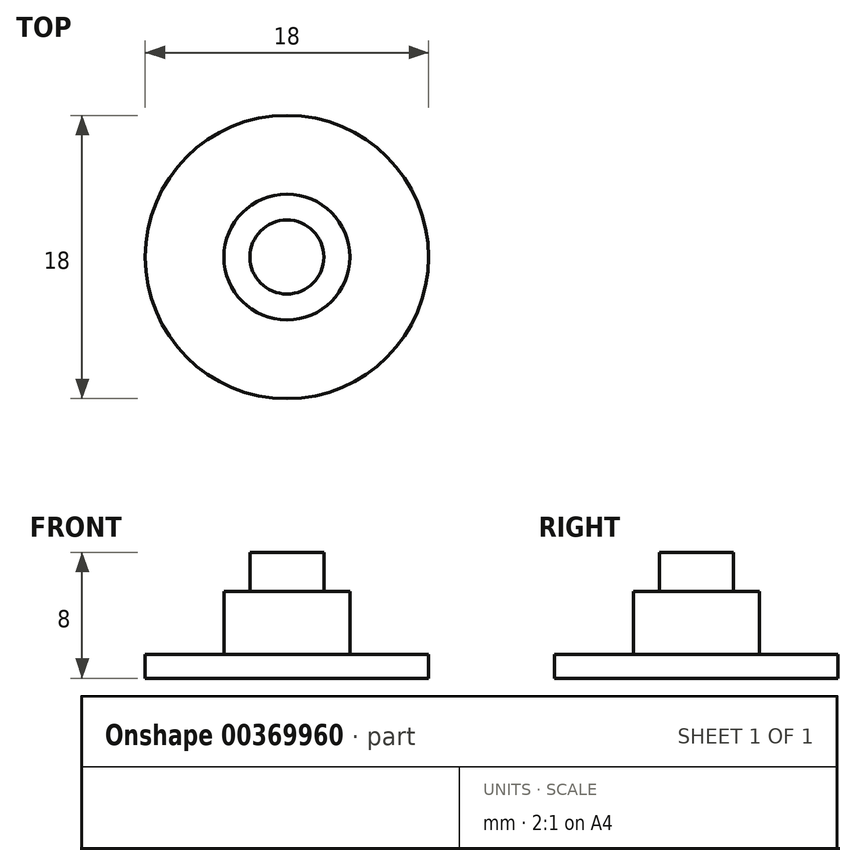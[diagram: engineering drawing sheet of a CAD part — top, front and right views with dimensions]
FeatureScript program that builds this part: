
annotation { "Feature Type Name" : "Feature", "Feature Type Description" : "" }
export const myFeature = defineFeature(function(context is Context, id is Id, definition is map)
    precondition{}
    {
        {
            var Q0;
            Q0=qCreatedBy(makeId("Top.planeOp"),FACE);
            var sketch = newSketch(context, id + "F0", { "sketchPlane" : qUnion([Q0])});
            skCircle(sketch, "E0", {"center": v(0, 0) * mm, "radius": 9 * mm});
            skCircle(sketch, "E1", {"center": v(0, 0) * mm, "radius": 4 * mm});
            skSolve(sketch);
        }
        {
            var Q0;
            Q0=makeQuery(id+"F0.imprint","IMPRINT",FACE,{"disambiguationData":[TD([[makeQuery(id+"F0.imprint","IMPRINT",EDGE,{"derivedFrom":sQuery(id+"F0.wireOp",EDGE,"E0")}),1.0]])]});
            var Q1;
            Q1=makeQuery(id+"F0.imprint","IMPRINT",FACE,{"disambiguationData":[TD([[makeQuery(id+"F0.imprint","IMPRINT",EDGE,{"derivedFrom":sQuery(id+"F0.wireOp",EDGE,"9xaSZKRW-TVAN-VkDE-0Sqe-EPZ7BEAft2Vu")}),1.0]])]});
            var Q2;
            Q2=makeQuery(id+"F0.imprint","IMPRINT",FACE,{"disambiguationData":[TD([[makeQuery(id+"F0.imprint","IMPRINT",EDGE,{"derivedFrom":sQuery(id+"F0.wireOp",EDGE,"9xaSZKRW-TVAN-VkDE-0Sqe-EPZ7BEAft2Vu")}),-1.0]])]});
            var Q3;
            Q3=makeQuery(id+"F0.imprint","IMPRINT",FACE,{"disambiguationData":[TD([[makeQuery(id+"F0.imprint","IMPRINT",EDGE,{"derivedFrom":sQuery(id+"F0.wireOp",EDGE,"E1")}),1.0]])]});
            extrude(context, id + "F1", {"entities" : qUnion([Q0, Q1, Q2, Q3]), "oppositeDirection" : true, "depth" : 1.5 * mm, "offsetDistance" : 25 * mm});
        }
        {
            var Q0;
            Q0=makeQuery(id+"F0.imprint","IMPRINT",FACE,{"disambiguationData":[TD([[makeQuery(id+"F0.imprint","IMPRINT",EDGE,{"derivedFrom":sQuery(id+"F0.wireOp",EDGE,"9xaSZKRW-TVAN-VkDE-0Sqe-EPZ7BEAft2Vu")}),1.0]])]});
            var Q1;
            Q1=makeQuery(id+"F0.imprint","IMPRINT",FACE,{"disambiguationData":[TD([[makeQuery(id+"F0.imprint","IMPRINT",EDGE,{"derivedFrom":sQuery(id+"F0.wireOp",EDGE,"9xaSZKRW-TVAN-VkDE-0Sqe-EPZ7BEAft2Vu")}),-1.0]])]});
            var Q2;
            Q2=makeQuery(id+"F0.imprint","IMPRINT",FACE,{"disambiguationData":[TD([[makeQuery(id+"F0.imprint","IMPRINT",EDGE,{"derivedFrom":sQuery(id+"F0.wireOp",EDGE,"E1")}),1.0]])]});
            extrude(context, id + "F2", {"entities" : qUnion([Q0, Q1, Q2]), "operationType" : NewBodyOperationType.ADD, "depth" : 4 * mm, "offsetDistance" : 25 * mm});
        }
        {
            var Q0;
            Q0=makeQuery(id+"F2.opExtrude","CAP_FACE",FACE,{"disambiguationData":[OSD([sQuery(id+"F0.wireOp",EDGE,"E1")])],"isStart":false});
            var sketch = newSketch(context, id + "F3", { "sketchPlane" : qUnion([Q0])});
            skCircle(sketch, "E2", {"center": v(0, 0) * mm, "radius": 2.35 * mm});
            skSolve(sketch);
        }
        {
            var Q0;
            Q0 = qSketchRegion(id + "F3", true);
            extrude(context, id + "F4", {"entities" : qUnion([Q0]), "operationType" : NewBodyOperationType.ADD, "depth" : 2.5 * mm, "offsetDistance" : 25 * mm});
        }
    });
